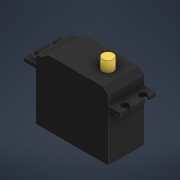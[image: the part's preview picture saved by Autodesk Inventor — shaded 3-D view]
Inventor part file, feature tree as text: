
AUTODESK INVENTOR PART (.ipt)
format: ipt  version: 2021 (Build 250183000, 183)  size: 165,888 bytes
history: native  units: mm
features: extrude x3, sketch x3
ambient origin geometry x8: Origin, YZ Plane, XZ Plane, XY Plane, X Axis, Y Axis, Z Axis, Center Point
bodies: Volumenkörper1 (feature_tree)
feature tree (6):
  extrude  "Extrusion1"  Depth=26.6mm
  extrude  "Extrusion2"  Depth=10.0mm
  extrude  "Extrusion3"  Depth=6.0mm
  sketch  "Skizze1"  dims[d0=40.3mm d1=26.6mm]
  sketch  "Skizze2"  dims[d3=10.0mm d4=3.618671mm]
  sketch  "Skizze3"  dims[d5=3.402944mm d6=3.241736mm d7=18.036317mm d8=24.84032mm d9=24.604189mm d10=6.65mm d11=2.0mm d12=6.65mm d13=2.0mm d17=20.0mm d18=0.0mm d19=4.0mm d21=5.0mm d23=2.5mm d25=2.0mm d26=20.0mm d27=0.0mm d28=6.0mm d29=10.0mm d30=6.0mm d31=0.0mm]
